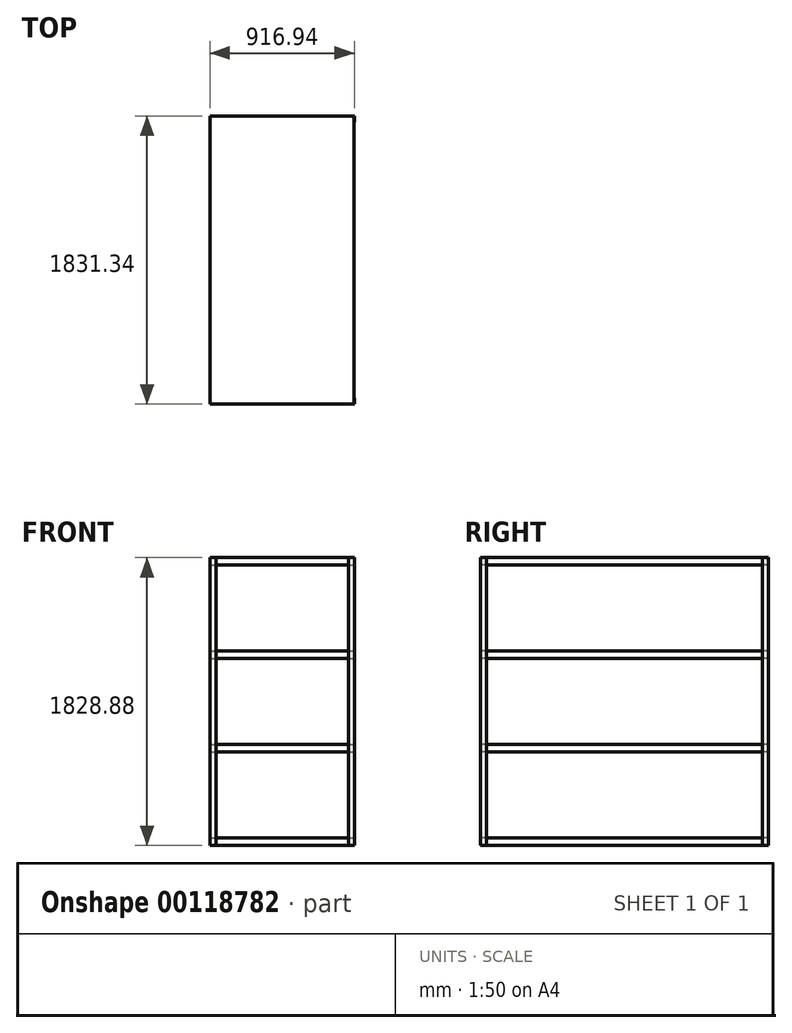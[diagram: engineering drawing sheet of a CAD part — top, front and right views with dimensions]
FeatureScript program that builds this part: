
annotation { "Feature Type Name" : "Feature", "Feature Type Description" : "" }
export const myFeature = defineFeature(function(context is Context, id is Id, definition is map)
    precondition{}
    {
        {
            var Q0;
            Q0=qCreatedBy(makeId("Top.planeOp"),FACE);
            var sketch = newSketch(context, id + "F0", { "sketchPlane" : qUnion([Q0])});
            skLineSegment(sketch, "E0.bottom", {"start": v(-457.2, 914.4) * mm, "end": v(457.2, 914.4) * mm});
            skLineSegment(sketch, "E0.top", {"start": v(-457.2, -914.4) * mm, "end": v(457.2, -914.4) * mm});
            skLineSegment(sketch, "E0.left", {"start": v(-457.2, 914.4) * mm, "end": v(-457.2, -914.4) * mm});
            skLineSegment(sketch, "E0.right", {"start": v(457.2, 914.4) * mm, "end": v(457.2, -914.4) * mm});
            skPoint(sketch, "E0.middle", {"position": v(0, 0) * mm});
            skSolve(sketch);
        }
        {
            var Q0;
            Q0 = qSketchRegion(id + "F0", true);
            extrude(context, id + "F1", {"entities" : qUnion([Q0]), "depth" : 47.62 * mm});
        }
        {
            var Q0;
            Q0=makeQuery(id+"F1.opExtrude","CAP_FACE",FACE,{"disambiguationData":[OSD([sQuery(id+"F0.wireOp",EDGE,"E0.bottom"),sQuery(id+"F0.wireOp",EDGE,"E0.top"),sQuery(id+"F0.wireOp",EDGE,"E0.left"),sQuery(id+"F0.wireOp",EDGE,"E0.right")])],"isStart":false});
            var sketch = newSketch(context, id + "F2", { "sketchPlane" : qUnion([Q0])});
            skLineSegment(sketch, "E1.bottom", {"start": v(-458.47, 915.67) * mm, "end": v(458.47, 915.67) * mm, "construction": true});
            skLineSegment(sketch, "E1.left", {"start": v(-458.47, 915.67) * mm, "end": v(-458.47, -915.67) * mm, "construction": true});
            skLineSegment(sketch, "E1.right", {"start": v(458.47, 915.67) * mm, "end": v(458.47, -915.67) * mm, "construction": true});
            skPoint(sketch, "E1.middle", {"position": v(0, 0) * mm});
            skLineSegment(sketch, "E2.left", {"start": v(-458.47, 915.67) * mm, "end": v(-458.47, 877.57) * mm, "construction": true});
            skLineSegment(sketch, "E3.top", {"start": v(420.37, -915.67) * mm, "end": v(458.47, -915.67) * mm, "construction": true});
            skLineSegment(sketch, "E3.left", {"start": v(420.37, 915.67) * mm, "end": v(420.37, -915.67) * mm, "construction": true});
            skLineSegment(sketch, "E4.bottom", {"start": v(458.47, -877.57) * mm, "end": v(-458.47, -877.57) * mm, "construction": true});
            skLineSegment(sketch, "E4.left", {"start": v(458.47, -877.57) * mm, "end": v(458.47, -920.76) * mm, "construction": true});
            skLineSegment(sketch, "E4.right", {"start": v(-458.47, -877.57) * mm, "end": v(-458.47, -915.67) * mm, "construction": true});
            skLineSegment(sketch, "E5", {"start": v(-458.47, -915.67) * mm, "end": v(420.37, -915.67) * mm, "construction": true});
            skLineSegment(sketch, "E6.bottom", {"start": v(458.47, 915.67) * mm, "end": v(-458.47, 915.67) * mm, "construction": true});
            skLineSegment(sketch, "E6.top", {"start": v(458.47, 877.57) * mm, "end": v(-458.47, 877.57) * mm, "construction": true});
            skLineSegment(sketch, "E6.left", {"start": v(458.47, 915.67) * mm, "end": v(458.47, 877.57) * mm, "construction": true});
            skLineSegment(sketch, "E7.bottom", {"start": v(-420.37, 915.67) * mm, "end": v(-458.47, 915.67) * mm, "construction": true});
            skLineSegment(sketch, "E7.top", {"start": v(-420.37, -915.67) * mm, "end": v(-458.47, -915.67) * mm, "construction": true});
            skLineSegment(sketch, "E7.left", {"start": v(-420.37, 915.67) * mm, "end": v(-420.37, -915.67) * mm, "construction": true});
            skLineSegment(sketch, "E8", {"start": v(458.47, -877.57) * mm, "end": v(457.2, -877.57) * mm});
            skLineSegment(sketch, "E9", {"start": v(457.2, -877.57) * mm, "end": v(457.2, -914.4) * mm});
            skLineSegment(sketch, "E10", {"start": v(457.2, -914.4) * mm, "end": v(420.37, -914.4) * mm});
            skLineSegment(sketch, "E11", {"start": v(420.37, -914.4) * mm, "end": v(420.37, -915.67) * mm});
            skLineSegment(sketch, "E12", {"start": v(458.47, -915.67) * mm, "end": v(420.37, -915.67) * mm});
            skLineSegment(sketch, "E13", {"start": v(458.47, -915.67) * mm, "end": v(458.47, -877.57) * mm});
            skLineSegment(sketch, "E14", {"start": v(-420.37, -915.67) * mm, "end": v(-420.37, -914.4) * mm});
            skLineSegment(sketch, "E15", {"start": v(-420.37, -914.4) * mm, "end": v(-457.2, -914.4) * mm});
            skLineSegment(sketch, "E16", {"start": v(-457.2, -914.4) * mm, "end": v(-457.2, -877.57) * mm});
            skLineSegment(sketch, "E17", {"start": v(-457.2, -877.57) * mm, "end": v(-458.47, -877.57) * mm});
            skLineSegment(sketch, "E18", {"start": v(-458.47, -877.57) * mm, "end": v(-458.47, -915.67) * mm});
            skLineSegment(sketch, "E19", {"start": v(-458.47, -915.67) * mm, "end": v(-420.37, -915.67) * mm});
            skLineSegment(sketch, "E20", {"start": v(-458.47, 877.57) * mm, "end": v(-457.2, 877.57) * mm});
            skLineSegment(sketch, "E21", {"start": v(-457.2, 877.57) * mm, "end": v(-457.2, 914.4) * mm});
            skLineSegment(sketch, "E22", {"start": v(-457.2, 914.4) * mm, "end": v(-420.37, 914.4) * mm});
            skLineSegment(sketch, "E23", {"start": v(-420.37, 914.4) * mm, "end": v(-420.37, 915.67) * mm});
            skLineSegment(sketch, "E24", {"start": v(-420.37, 915.67) * mm, "end": v(-458.47, 915.67) * mm});
            skLineSegment(sketch, "E25", {"start": v(-458.47, 915.67) * mm, "end": v(-458.47, 877.57) * mm});
            skLineSegment(sketch, "E26", {"start": v(420.37, 915.67) * mm, "end": v(458.47, 915.67) * mm});
            skLineSegment(sketch, "E27", {"start": v(458.47, 915.67) * mm, "end": v(458.47, 877.57) * mm});
            skLineSegment(sketch, "E28", {"start": v(458.47, 877.57) * mm, "end": v(457.2, 877.57) * mm});
            skLineSegment(sketch, "E29", {"start": v(457.2, 877.57) * mm, "end": v(457.2, 914.4) * mm});
            skLineSegment(sketch, "E30", {"start": v(457.2, 914.4) * mm, "end": v(420.37, 914.4) * mm});
            skLineSegment(sketch, "E31", {"start": v(420.37, 914.4) * mm, "end": v(420.37, 915.67) * mm});
            skSolve(sketch);
        }
        {
            var Q0;
            Q0 = qSketchRegion(id + "F2", true);
            extrude(context, id + "F3", {"entities" : qUnion([Q0]), "operationType" : NewBodyOperationType.ADD, "depth" : 1781.17 * mm, "hasSecondDirection" : true, "secondDirectionOppositeDirection" : true, "secondDirectionDepth" : 47.62 * mm});
        }
        {
            var Q0;
            Q0=makeQuery(id+"F1.opExtrude","CAP_FACE",FACE,{"disambiguationData":[OSD([sQuery(id+"F0.wireOp",EDGE,"E0.bottom"),sQuery(id+"F0.wireOp",EDGE,"E0.top"),sQuery(id+"F0.wireOp",EDGE,"E0.left"),sQuery(id+"F0.wireOp",EDGE,"E0.right")])],"isStart":false});
            cPlane(context, id + "F4", {"entities" : qUnion([Q0]), "cplaneType" : CPlaneType.OFFSET, "offset" : 546.1 * mm, "width" : 152.4 * mm, "height" : 152.4 * mm});
        }
        {
            var Q0;
            Q0=qCreatedBy(id+"F4.planeOp",FACE);
            var sketch = newSketch(context, id + "F5", { "sketchPlane" : qUnion([Q0])});
            skLineSegment(sketch, "E32.bottom", {"start": v(-457.2, 914.4) * mm, "end": v(457.2, 914.4) * mm});
            skLineSegment(sketch, "E32.top", {"start": v(-457.2, -914.4) * mm, "end": v(457.2, -914.4) * mm});
            skLineSegment(sketch, "E32.left", {"start": v(-457.2, 914.4) * mm, "end": v(-457.2, -914.4) * mm});
            skLineSegment(sketch, "E32.right", {"start": v(457.2, 914.4) * mm, "end": v(457.2, -914.4) * mm});
            skPoint(sketch, "E32.middle", {"position": v(0, 0) * mm});
            skSolve(sketch);
        }
        {
            var Q0;
            Q0 = qSketchRegion(id + "F5", true);
            extrude(context, id + "F6", {"entities" : qUnion([Q0]), "operationType" : NewBodyOperationType.ADD, "depth" : 47.62 * mm});
        }
        {
            var Q0;
            Q0=makeQuery(id+"F6.opExtrude","CAP_FACE",FACE,{"disambiguationData":[OSD([sQuery(id+"F5.wireOp",EDGE,"E32.bottom"),sQuery(id+"F5.wireOp",EDGE,"E32.top"),sQuery(id+"F5.wireOp",EDGE,"E32.left"),sQuery(id+"F5.wireOp",EDGE,"E32.right")])],"isStart":false});
            cPlane(context, id + "F7", {"entities" : qUnion([Q0]), "cplaneType" : CPlaneType.OFFSET, "offset" : 546.1 * mm, "width" : 152.4 * mm, "height" : 152.4 * mm});
        }
        {
            var Q0;
            Q0=qCreatedBy(id+"F7.planeOp",FACE);
            var sketch = newSketch(context, id + "F8", { "sketchPlane" : qUnion([Q0])});
            skLineSegment(sketch, "E33.bottom", {"start": v(-457.2, 914.4) * mm, "end": v(457.2, 914.4) * mm});
            skLineSegment(sketch, "E33.top", {"start": v(-457.2, -914.4) * mm, "end": v(457.2, -914.4) * mm});
            skLineSegment(sketch, "E33.left", {"start": v(-457.2, 914.4) * mm, "end": v(-457.2, -914.4) * mm});
            skLineSegment(sketch, "E33.right", {"start": v(457.2, 914.4) * mm, "end": v(457.2, -914.4) * mm});
            skPoint(sketch, "E33.middle", {"position": v(0, 0) * mm});
            skSolve(sketch);
        }
        {
            var Q0;
            Q0 = qSketchRegion(id + "F8", true);
            extrude(context, id + "F9", {"entities" : qUnion([Q0]), "operationType" : NewBodyOperationType.ADD, "depth" : 47.62 * mm});
        }
        {
            var Q0;
            Q0=makeQuery(id+"F9.opExtrude","CAP_FACE",FACE,{"disambiguationData":[OSD([sQuery(id+"F8.wireOp",EDGE,"E33.bottom"),sQuery(id+"F8.wireOp",EDGE,"E33.top"),sQuery(id+"F8.wireOp",EDGE,"E33.left"),sQuery(id+"F8.wireOp",EDGE,"E33.right")])],"isStart":false});
            cPlane(context, id + "F10", {"entities" : qUnion([Q0]), "cplaneType" : CPlaneType.OFFSET, "offset" : 546.1 * mm, "width" : 152.4 * mm, "height" : 152.4 * mm});
        }
        {
            var Q0;
            Q0=qCreatedBy(id+"F10.planeOp",FACE);
            var sketch = newSketch(context, id + "F11", { "sketchPlane" : qUnion([Q0])});
            skLineSegment(sketch, "E34.bottom", {"start": v(-457.2, 914.4) * mm, "end": v(457.2, 914.4) * mm});
            skLineSegment(sketch, "E34.top", {"start": v(-457.2, -914.4) * mm, "end": v(457.2, -914.4) * mm});
            skLineSegment(sketch, "E34.left", {"start": v(-457.2, 914.4) * mm, "end": v(-457.2, -914.4) * mm});
            skLineSegment(sketch, "E34.right", {"start": v(457.2, 914.4) * mm, "end": v(457.2, -914.4) * mm});
            skPoint(sketch, "E34.middle", {"position": v(0, 0) * mm});
            skSolve(sketch);
        }
        {
            var Q0;
            Q0 = qSketchRegion(id + "F11", true);
            extrude(context, id + "F12", {"entities" : qUnion([Q0]), "operationType" : NewBodyOperationType.ADD, "depth" : 47.7 * mm});
        }
    });
